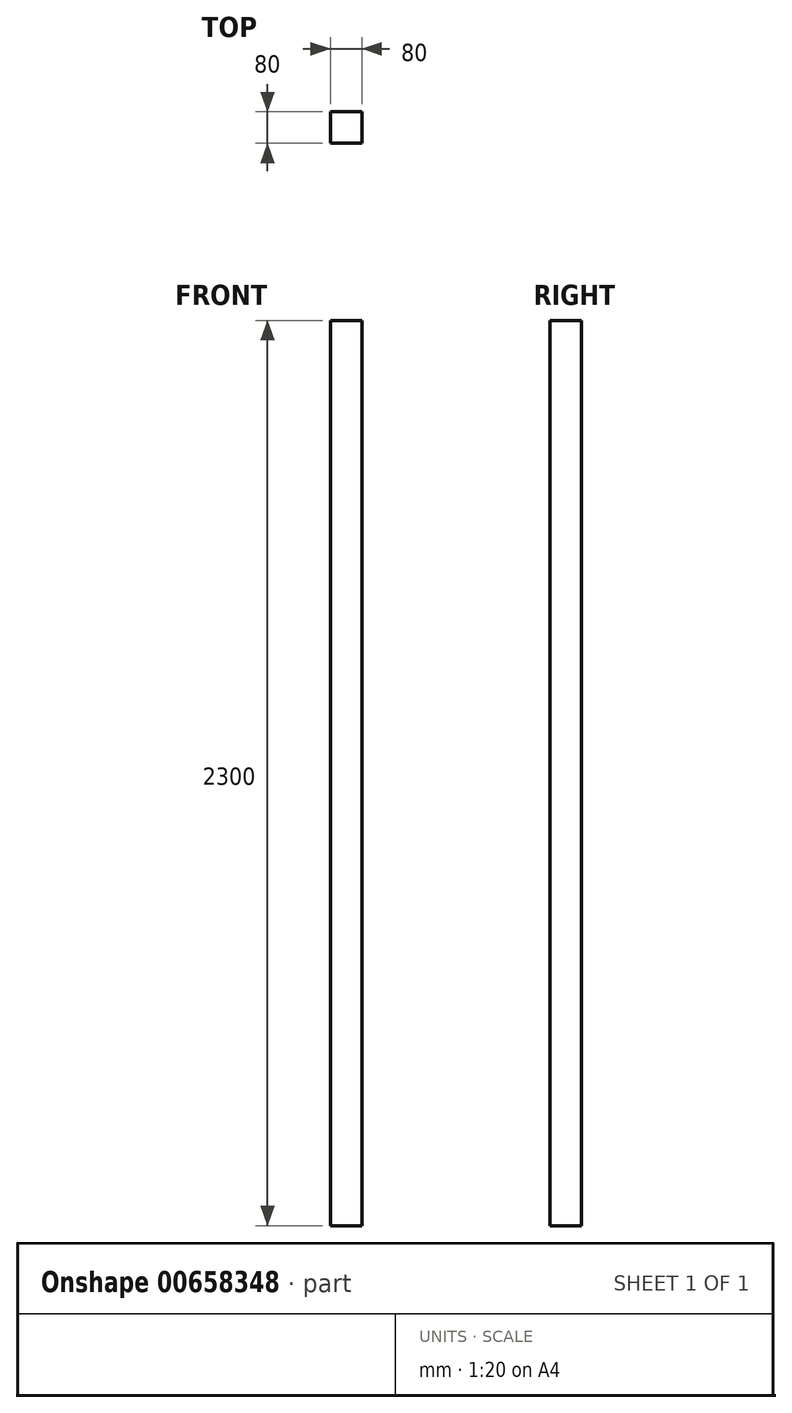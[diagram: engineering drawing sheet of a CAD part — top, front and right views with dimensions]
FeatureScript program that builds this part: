
annotation { "Feature Type Name" : "Feature", "Feature Type Description" : "" }
export const myFeature = defineFeature(function(context is Context, id is Id, definition is map)
    precondition{}
    {
        {
            var Q0;
            Q0=qCreatedBy(makeId("Top.planeOp"),FACE);
            var sketch = newSketch(context, id + "F0", { "sketchPlane" : qUnion([Q0])});
            skLineSegment(sketch, "E0.bottom", {"start": v(-45, 24.68) * mm, "end": v(35, 24.68) * mm});
            skLineSegment(sketch, "E0.top", {"start": v(-45, -55.32) * mm, "end": v(35, -55.32) * mm});
            skLineSegment(sketch, "E0.left", {"start": v(-45, 24.68) * mm, "end": v(-45, -55.32) * mm});
            skLineSegment(sketch, "E0.right", {"start": v(35, 24.68) * mm, "end": v(35, -55.32) * mm});
            skSolve(sketch);
        }
        {
            var Q0;
            Q0 = qSketchRegion(id + "F0", true);
            var Q1;
            Q1 = qSketchRegion(id + "F2", true);
            extrude(context, id + "F1", {"entities" : qUnion([Q0, Q1]), "depth" : 2300 * mm, "offsetDistance" : 25 * mm});
        }
    });
